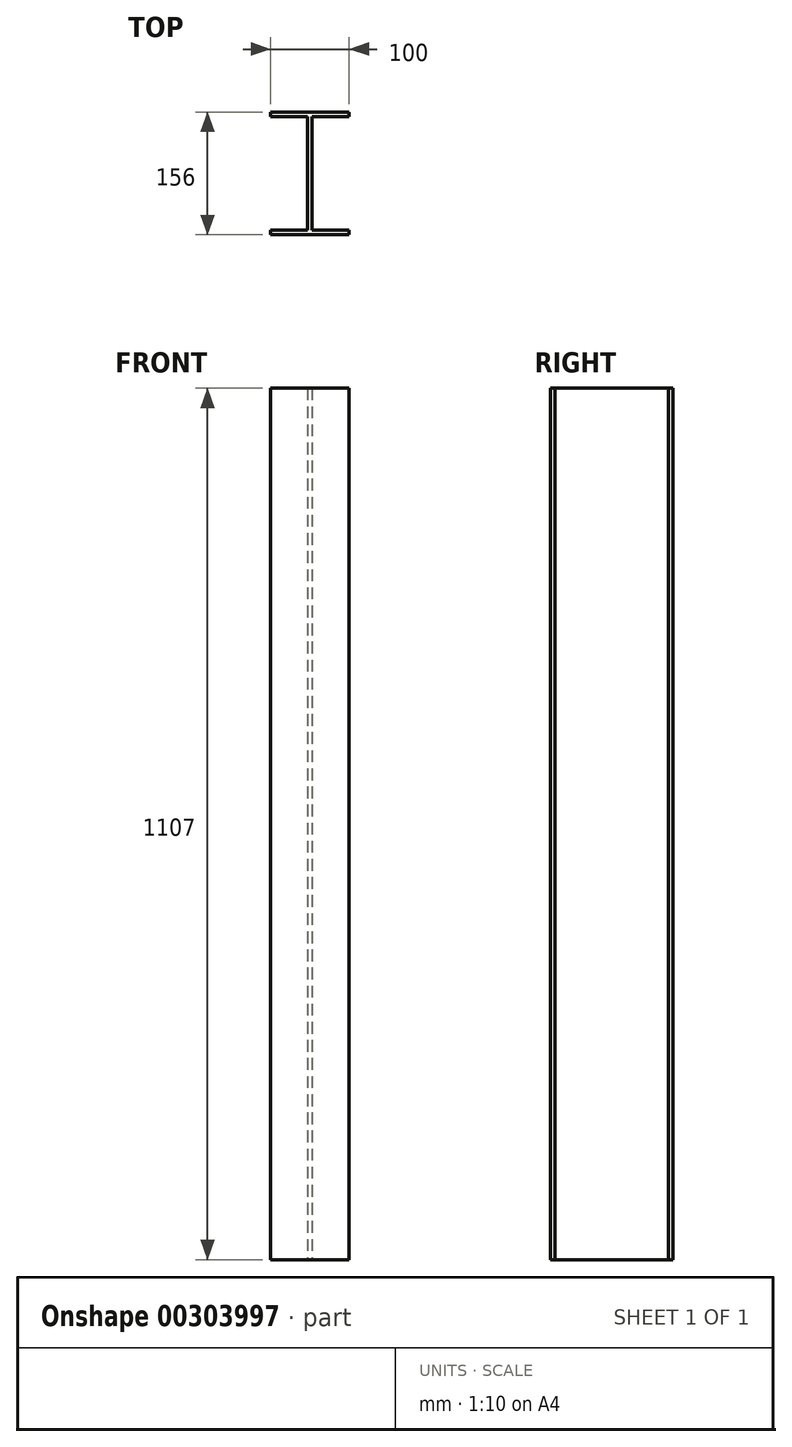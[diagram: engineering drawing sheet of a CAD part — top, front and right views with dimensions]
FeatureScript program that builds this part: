
annotation { "Feature Type Name" : "Feature", "Feature Type Description" : "" }
export const myFeature = defineFeature(function(context is Context, id is Id, definition is map)
    precondition{}
    {
        {
            var Q0;
            Q0=qCreatedBy(makeId("Top.planeOp"),FACE);
            var sketch = newSketch(context, id + "F0", { "sketchPlane" : qUnion([Q0])});
            skLineSegment(sketch, "E0", {"start": v(-47.96, 88.22) * mm, "end": v(52.04, 88.22) * mm});
            skLineSegment(sketch, "E1", {"start": v(52.04, 88.22) * mm, "end": v(52.04, 82.22) * mm});
            skLineSegment(sketch, "E2", {"start": v(52.04, 82.22) * mm, "end": v(5.04, 82.22) * mm});
            skLineSegment(sketch, "E3", {"start": v(5.04, 82.22) * mm, "end": v(5.04, -61.78) * mm});
            skLineSegment(sketch, "E4", {"start": v(5.04, -61.78) * mm, "end": v(52.04, -61.78) * mm});
            skLineSegment(sketch, "E5", {"start": v(52.04, -61.78) * mm, "end": v(52.04, -67.78) * mm});
            skLineSegment(sketch, "E6", {"start": v(52.04, -67.78) * mm, "end": v(-47.96, -67.78) * mm});
            skLineSegment(sketch, "E7", {"start": v(-47.96, -67.78) * mm, "end": v(-47.96, -61.78) * mm});
            skLineSegment(sketch, "E8", {"start": v(-47.96, -61.78) * mm, "end": v(-0.96, -61.78) * mm});
            skLineSegment(sketch, "E9", {"start": v(-0.96, -61.78) * mm, "end": v(-0.96, 82.22) * mm});
            skLineSegment(sketch, "E10", {"start": v(-0.96, 82.22) * mm, "end": v(-47.96, 82.22) * mm});
            skLineSegment(sketch, "E11", {"start": v(-47.96, 82.22) * mm, "end": v(-47.96, 88.22) * mm});
            skSolve(sketch);
        }
        {
            var Q0;
            Q0 = qSketchRegion(id + "F0", true);
            extrude(context, id + "F1", {"entities" : qUnion([Q0]), "depth" : 107 * mm, "offsetDistance" : 25 * mm, "hasSecondDirection" : true, "secondDirectionOppositeDirection" : true, "secondDirectionDepth" : 1000 * mm});
        }
    });
